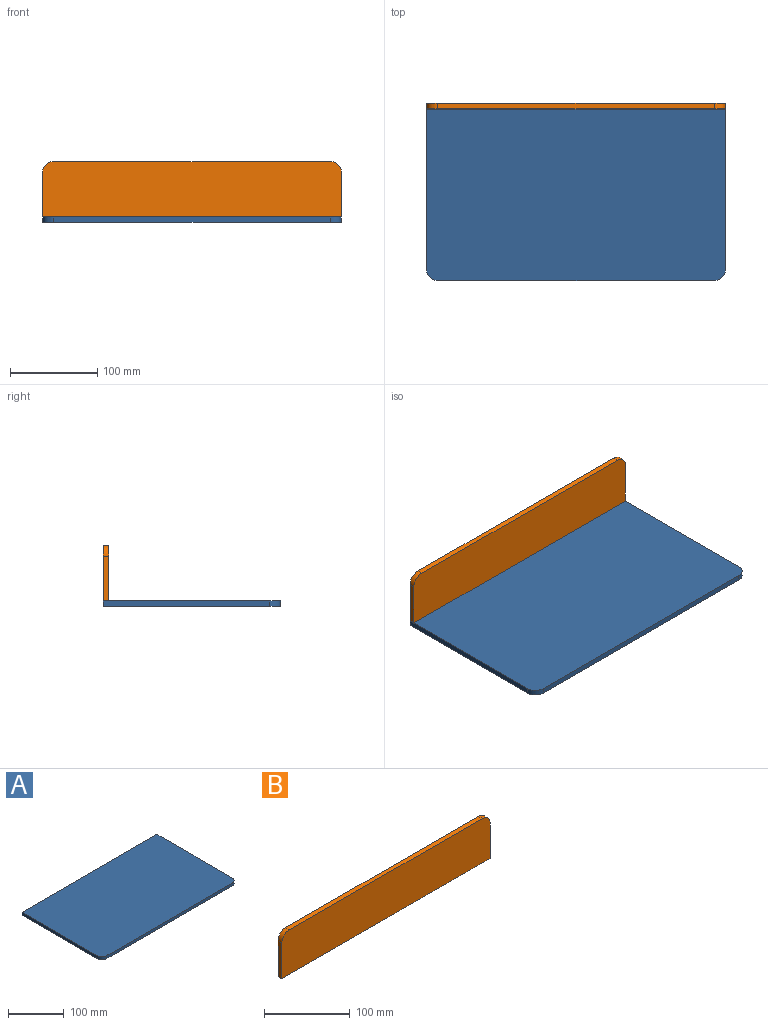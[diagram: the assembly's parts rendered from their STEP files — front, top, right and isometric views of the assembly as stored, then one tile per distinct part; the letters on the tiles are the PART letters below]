
ASSEMBLY  parts=2 mates=1
PART A: 8 faces, bbox 342.9x203.2x6.4 mm
  f0: plane 190.5x6.35mm, normal (-1,0,0), area 1209.7mm2, adj f3,f4,f5,f6
  f1: plane 317.5x6.35mm, normal (0,-1,0), area 2016.1mm2, adj f4,f5,f6,f7
  f2: plane 190.5x6.35mm, normal (1,0,0), area 1209.7mm2, adj f3,f4,f5,f7
  f3: plane 342.9x6.35mm, normal (0,1,0), area 2177.4mm2, adj f0,f2,f4,f5
  f4: plane 342.9x203.2mm, normal (0,0,1), area 69608.1mm2, adj f0,f1,f2,f3,f6,f7
  f5: plane 342.9x203.2mm, normal (0,0,-1), area 69608.1mm2, adj f0,f1,f2,f3,f6,f7
  f6: cylinder r=12.7mm len=12.7mm, axis (0,0,-1), area 126.7mm2, adj f0,f1,f4,f5
  f7: cylinder r=12.7mm len=12.7mm, axis (0,0,1), area 126.7mm2, adj f1,f2,f4,f5
PART B: 8 faces, bbox 342.9x6.4x63.5 mm
  f0: plane 50.8x6.35mm, normal (-1,0,0), area 322.6mm2, adj f1,f4,f5,f7
  f1: plane 342.9x6.35mm, normal (0,0,-1), area 2177.4mm2, adj f0,f2,f4,f5
  f2: plane 50.8x6.35mm, normal (1,0,0), area 322.6mm2, adj f1,f4,f5,f6
  f3: plane 317.5x6.35mm, normal (0,0,1), area 2016.1mm2, adj f4,f5,f6,f7
  f4: plane 342.9x63.5mm, normal (0,-1,0), area 21704.9mm2, adj f0,f1,f2,f3,f6,f7
  f5: plane 342.9x63.5mm, normal (0,1,0), area 21704.9mm2, adj f0,f1,f2,f3,f6,f7
  f6: cylinder r=12.7mm len=12.7mm, axis (0,1,0), area 126.7mm2, adj f2,f3,f4,f5
  f7: cylinder r=12.7mm len=12.7mm, axis (0,-1,0), area 126.7mm2, adj f0,f3,f4,f5
PLACE A t=(-20.98,-8.82,-90.13)mm
PLACE B t=(-20.98,92.78,-52.03)mm
MATE fastened A.f4 <-> B.f1  axis (0,0,1) through (-20.98,92.78,-83.78)mm
